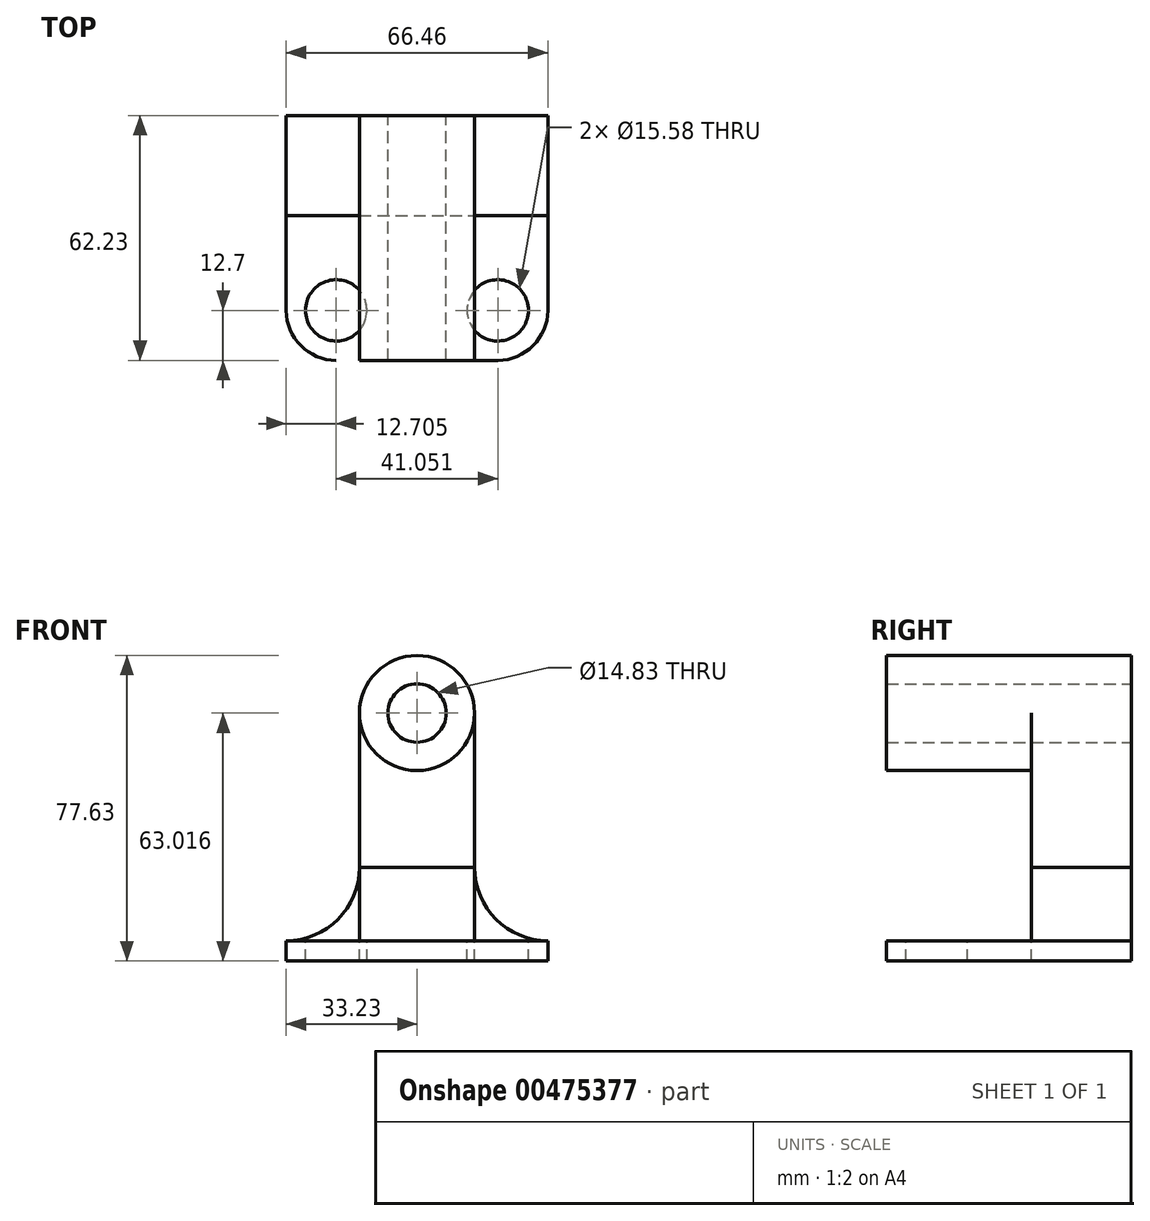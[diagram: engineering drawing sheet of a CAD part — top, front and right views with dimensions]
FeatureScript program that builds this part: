
annotation { "Feature Type Name" : "Feature", "Feature Type Description" : "" }
export const myFeature = defineFeature(function(context is Context, id is Id, definition is map)
    precondition{}
    {
        {
            var Q0;
            Q0=qCreatedBy(makeId("Front.planeOp"),FACE);
            var sketch = newSketch(context, id + "F0", { "sketchPlane" : qUnion([Q0])});
            skLineSegment(sketch, "E0.bottom", {"start": v(14.61, -31.5) * mm, "end": v(-14.61, -31.5) * mm});
            skLineSegment(sketch, "E0.top", {"start": v(14.61, 31.5) * mm, "end": v(-14.61, 31.5) * mm});
            skLineSegment(sketch, "E0.left", {"start": v(14.61, -31.5) * mm, "end": v(14.61, 31.5) * mm});
            skLineSegment(sketch, "E0.right", {"start": v(-14.61, -31.5) * mm, "end": v(-14.61, 31.5) * mm});
            skPoint(sketch, "E0.middle", {"position": v(0, 0) * mm});
            skCircle(sketch, "E1", {"center": v(0, 31.5) * mm, "radius": 14.61 * mm});
            skCircle(sketch, "E2", {"center": v(0, 31.5) * mm, "radius": 7.42 * mm});
            skLineSegment(sketch, "E3.bottom", {"start": v(-33.23, -31.5) * mm, "end": v(33.23, -31.5) * mm});
            skLineSegment(sketch, "E3.top", {"start": v(-14.61, -7.72) * mm, "end": v(14.61, -7.72) * mm});
            skLineSegment(sketch, "E3.left", {"start": v(-33.23, -31.5) * mm, "end": v(-33.23, -26.34) * mm});
            skLineSegment(sketch, "E3.right", {"start": v(33.23, -31.5) * mm, "end": v(33.23, -26.34) * mm});
            skArc(sketch, "E4", {"start": v(14.61, -7.72) * mm, "mid": v(20.06, -20.89) * mm, "end": v(33.23, -26.34) * mm});
            skArc(sketch, "E5", {"start": v(-33.23, -26.34) * mm, "mid": v(-20.06, -20.89) * mm, "end": v(-14.61, -7.72) * mm});
            skSolve(sketch);
        }
        {
            var Q0;
            {var subQ1=sQuery(id+"F0.wireOp",EDGE,"E0.top");var subQ3=sQuery(id+"F0.wireOp",EDGE,"E2");var subQ4=makeQuery(id+"F0.imprint","INTERSECT",VERTEX,{"disambiguationData":[OD(0.0)],"derivedFrom":[subQ1,subQ3]});Q0=makeQuery(id+"F0.imprint","IMPRINT",FACE,{"disambiguationData":[TD([[makeQuery(id+"F0.imprint","IMPRINT",EDGE,{"disambiguationData":[TD([[subQ4,-1.0]])],"derivedFrom":subQ3}),-1.0]])]});}
            var Q1;
            {var subQ0=sQuery(id+"F0.wireOp",EDGE,"E3.bottom");var subQ1=sQuery(id+"F0.wireOp",EDGE,"E0.left");var subQ2=makeQuery(id+"F0.imprint","INTERSECT",VERTEX,{"derivedFrom":[subQ1,subQ0]});Q1=makeQuery(id+"F0.imprint","IMPRINT",FACE,{"disambiguationData":[TD([[makeQuery(id+"F0.imprint","IMPRINT",EDGE,{"disambiguationData":[TD([[subQ2,-1.0]])],"derivedFrom":subQ0}),1.0]])]});}
            var Q2;
            {var subQ0=sQuery(id+"F0.wireOp",EDGE,"E1");var subQ1=sQuery(id+"F0.wireOp",EDGE,"E0.left");var subQ2=sQuery(id+"F0.wireOp",EDGE,"E0.top");var subQ3=makeQuery(id+"F0.imprint","INTERSECT",VERTEX,{"derivedFrom":[subQ2,subQ1,subQ0]});Q2=makeQuery(id+"F0.imprint","IMPRINT",FACE,{"disambiguationData":[TD([[makeQuery(id+"F0.imprint","IMPRINT",EDGE,{"disambiguationData":[TD([[subQ3,1.0]])],"derivedFrom":subQ1}),1.0]])]});}
            var Q3;
            {var subQ0=sQuery(id+"F0.wireOp",EDGE,"E3.bottom");var subQ1=sQuery(id+"F0.wireOp",EDGE,"E0.right");var subQ2=makeQuery(id+"F0.imprint","INTERSECT",VERTEX,{"derivedFrom":[subQ1,subQ0]});Q3=makeQuery(id+"F0.imprint","IMPRINT",FACE,{"disambiguationData":[TD([[makeQuery(id+"F0.imprint","IMPRINT",EDGE,{"disambiguationData":[TD([[subQ2,1.0]])],"derivedFrom":subQ0}),1.0]])]});}
            var Q4;
            {var subQ1=sQuery(id+"F0.wireOp",EDGE,"E0.top");var subQ3=sQuery(id+"F0.wireOp",EDGE,"E2");var subQ4=makeQuery(id+"F0.imprint","INTERSECT",VERTEX,{"disambiguationData":[OD(0.0)],"derivedFrom":[subQ1,subQ3]});Q4=makeQuery(id+"F0.imprint","IMPRINT",FACE,{"disambiguationData":[TD([[makeQuery(id+"F0.imprint","IMPRINT",EDGE,{"disambiguationData":[TD([[subQ4,1.0]])],"derivedFrom":subQ3}),-1.0]])]});}
            var Q5;
            {var subQ0=sQuery(id+"F0.wireOp",EDGE,"E3.bottom");var subQ1=sQuery(id+"F0.wireOp",EDGE,"E0.left");var subQ2=makeQuery(id+"F0.imprint","INTERSECT",VERTEX,{"derivedFrom":[subQ1,subQ0]});Q5=makeQuery(id+"F0.imprint","IMPRINT",FACE,{"disambiguationData":[TD([[makeQuery(id+"F0.imprint","IMPRINT",EDGE,{"disambiguationData":[TD([[subQ2,1.0]])],"derivedFrom":subQ0}),1.0]])]});}
            extrude(context, id + "F1", {"entities" : qUnion([Q0, Q1, Q2, Q3, Q4, Q5]), "depth" : 25.4 * mm});
        }
        {
            var Q0;
            Q0=makeQuery(id+"F1.opExtrude","CAP_FACE",FACE,{"disambiguationData":[OSD([sQuery(id+"F0.wireOp",EDGE,"E0.left"),sQuery(id+"F0.wireOp",EDGE,"E0.right"),sQuery(id+"F0.wireOp",EDGE,"E1"),sQuery(id+"F0.wireOp",EDGE,"E2"),sQuery(id+"F0.wireOp",EDGE,"E3.bottom"),sQuery(id+"F0.wireOp",EDGE,"E3.left"),sQuery(id+"F0.wireOp",EDGE,"E3.right"),sQuery(id+"F0.wireOp",EDGE,"E4"),sQuery(id+"F0.wireOp",EDGE,"E5")])],"isStart":false});
            var sketch = newSketch(context, id + "F2", { "sketchPlane" : qUnion([Q0])});
            skCircle(sketch, "E6", {"center": v(0, 31.5) * mm, "radius": 14.61 * mm});
            skCircle(sketch, "E7", {"center": v(0, 31.5) * mm, "radius": 7.42 * mm});
            skSolve(sketch);
        }
        {
            var Q0;
            Q0 = qSketchRegion(id + "F2", true);
            extrude(context, id + "F3", {"entities" : qUnion([Q0]), "operationType" : NewBodyOperationType.ADD, "depth" : 17.02 * mm});
        }
        {
            var Q0;
            Q0=makeQuery(id+"F1.opExtrude","CAP_FACE",FACE,{"disambiguationData":[OSD([sQuery(id+"F0.wireOp",EDGE,"E0.left"),sQuery(id+"F0.wireOp",EDGE,"E0.right"),sQuery(id+"F0.wireOp",EDGE,"E1"),sQuery(id+"F0.wireOp",EDGE,"E2"),sQuery(id+"F0.wireOp",EDGE,"E3.bottom"),sQuery(id+"F0.wireOp",EDGE,"E3.left"),sQuery(id+"F0.wireOp",EDGE,"E3.right"),sQuery(id+"F0.wireOp",EDGE,"E4"),sQuery(id+"F0.wireOp",EDGE,"E5")])],"isStart":false});
            var sketch = newSketch(context, id + "F4", { "sketchPlane" : qUnion([Q0])});
            skLineSegment(sketch, "E8.bottom", {"start": v(-33.23, -31.5) * mm, "end": v(33.23, -31.5) * mm});
            skLineSegment(sketch, "E8.top", {"start": v(-33.23, -26.34) * mm, "end": v(33.23, -26.34) * mm});
            skLineSegment(sketch, "E8.left", {"start": v(-33.23, -31.5) * mm, "end": v(-33.23, -26.34) * mm});
            skLineSegment(sketch, "E8.right", {"start": v(33.23, -31.5) * mm, "end": v(33.23, -26.34) * mm});
            skSolve(sketch);
        }
        {
            var Q0;
            Q0 = qSketchRegion(id + "F4", true);
            extrude(context, id + "F5", {"entities" : qUnion([Q0]), "operationType" : NewBodyOperationType.ADD, "depth" : 36.83 * mm});
        }
        {
            var Q0;
            Q0=makeQuery(id+"F5.opExtrude","CAP_EDGE",EDGE,{"disambiguationData":[OSD([sQuery(id+"F4.wireOp",EDGE,"E8.left")])],"isStart":false});
            var Q1;
            Q1=makeQuery(id+"F5.opExtrude","CAP_EDGE",EDGE,{"disambiguationData":[OSD([sQuery(id+"F4.wireOp",EDGE,"E8.right")])],"isStart":false});
            fillet(context, id + "F6", {"entities" : qUnion([Q0, Q1]), "radius" : 12.7 * mm, "tangentPropagation" : true, "allowEdgeOverflow" : false});
        }
        {
            var Q0;
            Q0=makeQuery(id+"F5.opExtrude","SWEPT_FACE",FACE,{"disambiguationData":[OSD([sQuery(id+"F4.wireOp",EDGE,"E8.top")])]});
            var sketch = newSketch(context, id + "F7", { "sketchPlane" : qUnion([Q0])});
            skCircle(sketch, "E9", {"center": v(-20.53, -49.53) * mm, "radius": 7.8 * mm});
            skCircle(sketch, "E10", {"center": v(20.53, -49.53) * mm, "radius": 7.8 * mm});
            skSolve(sketch);
        }
        {
            var Q0;
            Q0 = qSketchRegion(id + "F7", true);
            extrude(context, id + "F8", {"entities" : qUnion([Q0]), "operationType" : NewBodyOperationType.REMOVE, "endBound" : BoundingType.THROUGH_ALL, "oppositeDirection" : true, "depth" : 25.4 * mm});
        }
        {
            var Q0;
            Q0=makeQuery(id+"F3.opExtrude","CAP_FACE",FACE,{"disambiguationData":[OSD([sQuery(id+"F2.wireOp",EDGE,"E6"),sQuery(id+"F2.wireOp",EDGE,"E7")])],"isStart":false});
            var Q1;
            Q1=makeQuery(id+"F5.opExtrude","CAP_FACE",FACE,{"disambiguationData":[OSD([sQuery(id+"F4.wireOp",EDGE,"E8.bottom"),sQuery(id+"F4.wireOp",EDGE,"E8.top"),sQuery(id+"F4.wireOp",EDGE,"E8.left"),sQuery(id+"F4.wireOp",EDGE,"E8.right")])],"isStart":false});
            extrude(context, id + "F9", {"entities" : qUnion([Q0]), "operationType" : NewBodyOperationType.ADD, "endBound" : BoundingType.UP_TO_SURFACE, "endBoundEntityFace" : qUnion([Q1]), "depth" : 25.4 * mm});
        }
    });
